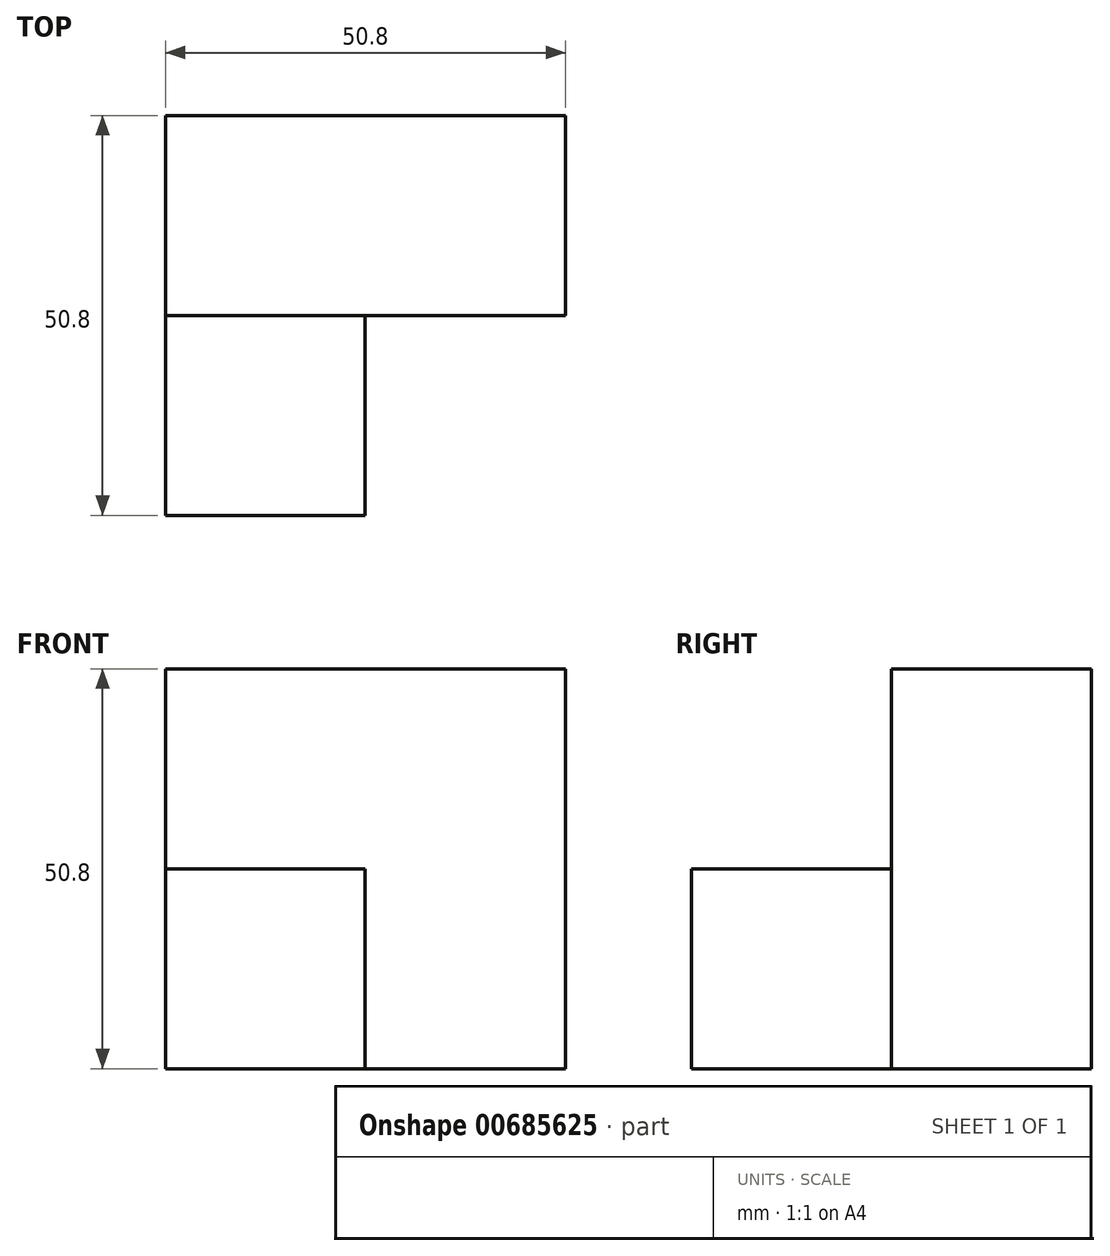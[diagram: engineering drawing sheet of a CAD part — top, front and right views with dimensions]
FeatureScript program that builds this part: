
annotation { "Feature Type Name" : "Feature", "Feature Type Description" : "" }
export const myFeature = defineFeature(function(context is Context, id is Id, definition is map)
    precondition{}
    {
        {
            var Q0;
            Q0=qCreatedBy(makeId("Front.planeOp"),FACE);
            var sketch = newSketch(context, id + "F0", { "sketchPlane" : qUnion([Q0])});
            skLineSegment(sketch, "E0", {"start": v(-67.78, 50.8) * mm, "end": v(-67.78, 0) * mm});
            skLineSegment(sketch, "E1", {"start": v(-67.78, 0) * mm, "end": v(-16.98, 0) * mm});
            skLineSegment(sketch, "E2", {"start": v(-16.98, 0) * mm, "end": v(-16.98, 50.8) * mm});
            skLineSegment(sketch, "E3", {"start": v(-67.78, 50.8) * mm, "end": v(-16.98, 50.8) * mm});
            skSolve(sketch);
        }
        {
            var Q0;
            Q0=makeQuery(id+"F0.imprint","IMPRINT",FACE,{"disambiguationData":[TD([[makeQuery(id+"F0.imprint","IMPRINT",EDGE,{"derivedFrom":sQuery(id+"F0.wireOp",EDGE,"E0")}),1.0]])]});
            extrude(context, id + "F1", {"entities" : qUnion([Q0]), "depth" : 25.4 * mm, "offsetDistance" : 25.4 * mm});
        }
        {
            var Q0;
            Q0=makeQuery(id+"F1.opExtrude","CAP_FACE",FACE,{"disambiguationData":[OSD([sQuery(id+"F0.wireOp",EDGE,"E0"),sQuery(id+"F0.wireOp",EDGE,"E1"),sQuery(id+"F0.wireOp",EDGE,"E2"),sQuery(id+"F0.wireOp",EDGE,"E3")])],"isStart":false});
            var sketch = newSketch(context, id + "F2", { "sketchPlane" : qUnion([Q0])});
            skLineSegment(sketch, "E4", {"start": v(-42.42, 0) * mm, "end": v(-42.42, 25.4) * mm});
            skLineSegment(sketch, "E5", {"start": v(-67.78, 25.4) * mm, "end": v(-42.38, 25.4) * mm});
            skSolve(sketch);
        }
        {
            var Q0;
            {var subQ0=sQuery(id+"F2.wireOp",EDGE,"E4");Q0=makeQuery(id+"F2.imprint","IMPRINT",FACE,{"disambiguationData":[TD([[makeQuery(id+"F2.imprint","IMPRINT",EDGE,{"derivedFrom":subQ0}),1.0]])]});}
            extrude(context, id + "F3", {"entities" : qUnion([Q0]), "operationType" : NewBodyOperationType.ADD, "depth" : 25.4 * mm, "offsetDistance" : 25.4 * mm});
        }
    });
